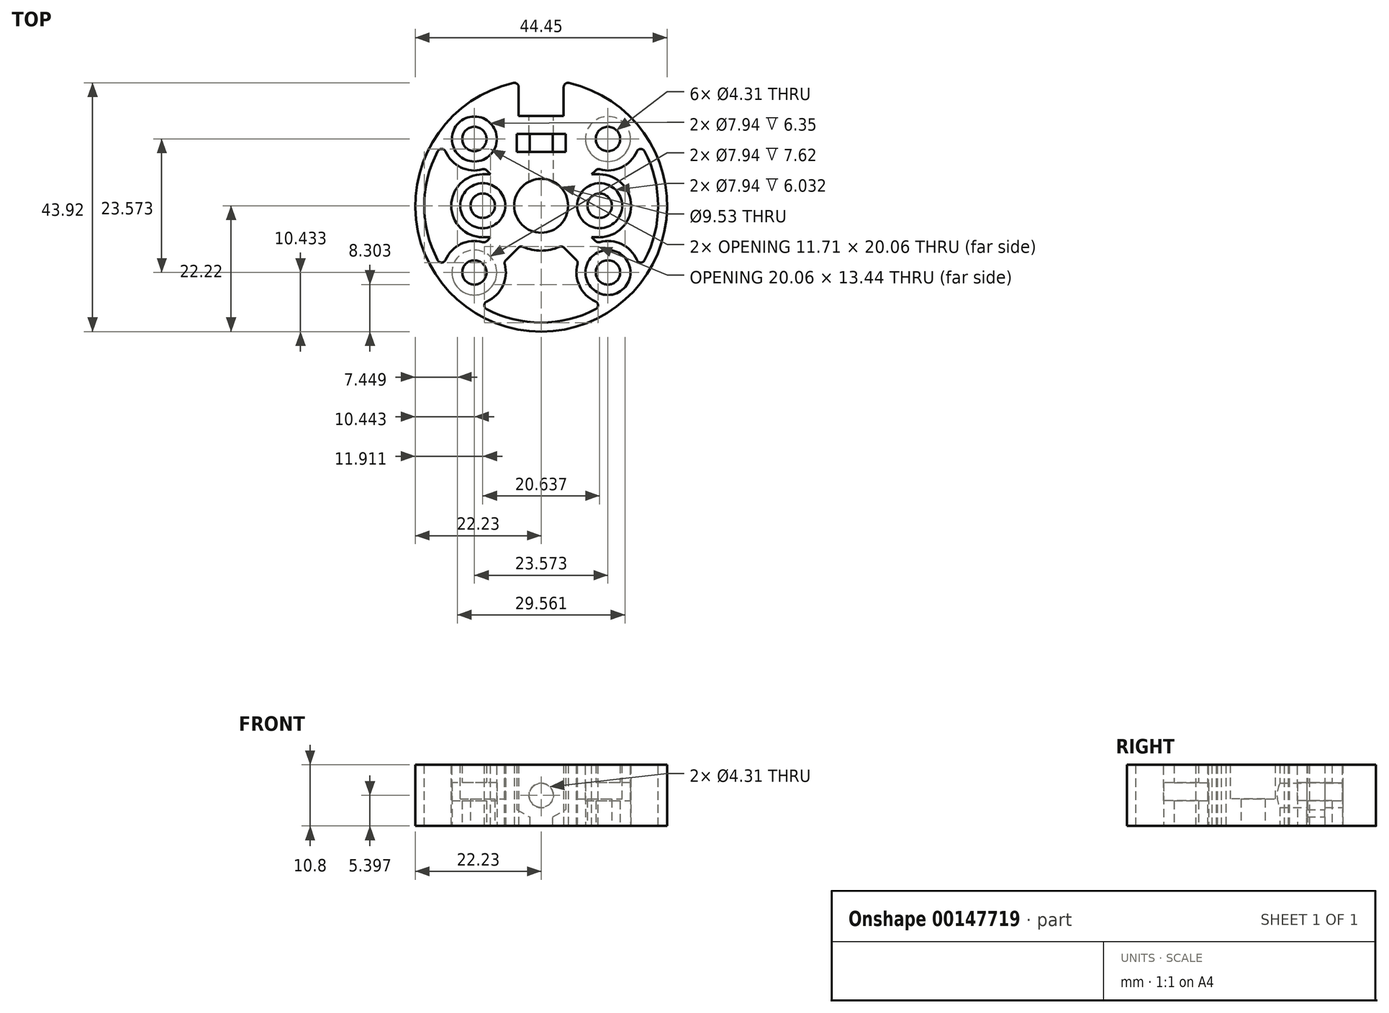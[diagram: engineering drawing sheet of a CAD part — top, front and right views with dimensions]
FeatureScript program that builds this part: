
annotation { "Feature Type Name" : "Feature", "Feature Type Description" : "" }
export const myFeature = defineFeature(function(context is Context, id is Id, definition is map)
    precondition{}
    {
        {
            var Q0;
            Q0=qCreatedBy(makeId("Top.planeOp"),FACE);
            var sketch = newSketch(context, id + "F0", { "sketchPlane" : qUnion([Q0])});
            skLineSegment(sketch, "E0.bottom", {"start": v(11.79, 11.79) * mm, "end": v(-11.79, 11.79) * mm, "construction": true});
            skLineSegment(sketch, "E0.top", {"start": v(11.79, -11.79) * mm, "end": v(-11.79, -11.79) * mm, "construction": true});
            skLineSegment(sketch, "E0.left", {"start": v(11.79, 11.79) * mm, "end": v(11.79, -11.79) * mm, "construction": true});
            skLineSegment(sketch, "E0.right", {"start": v(-11.79, 11.79) * mm, "end": v(-11.79, -11.79) * mm, "construction": true});
            skPoint(sketch, "E0.middle", {"position": v(0, 0) * mm});
            skCircle(sketch, "E1", {"center": v(-11.79, 11.79) * mm, "radius": 5.56 * mm, "construction": true});
            skLineSegment(sketch, "E2", {"start": v(0, 4.76) * mm, "end": v(0, 15.88) * mm});
            skLineSegment(sketch, "E3.bottom", {"start": v(-3.97, 21.87) * mm, "end": v(3.97, 21.87) * mm, "construction": true});
            skLineSegment(sketch, "E3.top", {"start": v(-3.97, 15.88) * mm, "end": v(3.97, 15.88) * mm});
            skLineSegment(sketch, "E3.left", {"start": v(-3.97, 21.87) * mm, "end": v(-3.97, 15.88) * mm});
            skLineSegment(sketch, "E3.right", {"start": v(3.97, 21.87) * mm, "end": v(3.97, 15.88) * mm});
            skArc(sketch, "E4", {"start": v(-3.97, 21.87) * mm, "mid": v(0, -22.22) * mm, "end": v(3.97, 21.87) * mm});
            skCircle(sketch, "E5", {"center": v(-11.79, 11.79) * mm, "radius": 2.15 * mm});
            skCircle(sketch, "E6", {"center": v(-11.79, -11.79) * mm, "radius": 2.15 * mm});
            skCircle(sketch, "E7", {"center": v(11.79, -11.79) * mm, "radius": 2.15 * mm});
            skCircle(sketch, "E8", {"center": v(11.79, 11.79) * mm, "radius": 2.15 * mm});
            skCircle(sketch, "E9", {"center": v(0, 0) * mm, "radius": 4.76 * mm});
            skLineSegment(sketch, "E10", {"start": v(0, 0) * mm, "end": v(0, 3.17) * mm, "construction": true});
            skLineSegment(sketch, "E11", {"start": v(0, 3.17) * mm, "end": v(0, 4.76) * mm, "construction": true});
            skLineSegment(sketch, "E12", {"start": v(-10.32, 0) * mm, "end": v(10.32, 0) * mm, "construction": true});
            skCircle(sketch, "E13", {"center": v(-10.32, 0) * mm, "radius": 2.15 * mm});
            skCircle(sketch, "E14", {"center": v(10.32, 0) * mm, "radius": 2.15 * mm});
            skSolve(sketch);
        }
        {
            var Q0;
            Q0=qSketchRegion(id+"F0",true);
            extrude(context, id + "F1", {"entities" : qUnion([Q0]), "depth" : 10.8 * mm});
        }
        {
            var Q0;
            Q0=makeQuery(id+"F1.opExtrude","SWEPT_FACE",FACE,{"disambiguationData":[OSD([sQuery(id+"F0.wireOp",EDGE,"E3.top")])]});
            var sketch = newSketch(context, id + "F2", { "sketchPlane" : qUnion([Q0])});
            skLineSegment(sketch, "E15", {"start": v(0, 10.8) * mm, "end": v(0, 0) * mm, "construction": true});
            skCircle(sketch, "E16", {"center": v(0, 5.4) * mm, "radius": 2.15 * mm});
            skSolve(sketch);
        }
        {
            var Q0;
            Q0=qSketchRegion(id+"F2",true);
            var Q1;
            Q1=makeQuery(id+"F1.opExtrude","SWEPT_FACE",FACE,{"disambiguationData":[OSD([sQuery(id+"F0.wireOp",EDGE,"E9")])]});
            extrude(context, id + "F3", {"entities" : qUnion([Q0]), "operationType" : NewBodyOperationType.REMOVE, "endBound" : BoundingType.UP_TO_SURFACE, "oppositeDirection" : true, "endBoundEntityFace" : qUnion([Q1]), "depth" : 25.4 * mm});
        }
        {
            var Q0;
            Q0=makeQuery(id+"F1.opExtrude","CAP_FACE",FACE,{"disambiguationData":[OSD([sQuery(id+"F0.wireOp",EDGE,"zcYoioO2-fyPR-UuhC-Hgss-rbXFzuCLLck7"),sQuery(id+"F0.wireOp",EDGE,"E3.top"),sQuery(id+"F0.wireOp",EDGE,"E3.left"),sQuery(id+"F0.wireOp",EDGE,"E3.right"),sQuery(id+"F0.wireOp",EDGE,"E4"),sQuery(id+"F0.wireOp",EDGE,"E5"),sQuery(id+"F0.wireOp",EDGE,"E6"),sQuery(id+"F0.wireOp",EDGE,"E7"),sQuery(id+"F0.wireOp",EDGE,"E8")])],"isStart":true});
            cPlane(context, id + "F4", {"entities" : qUnion([Q0]), "cplaneType" : CPlaneType.OFFSET, "offset" : 4.44 * mm, "oppositeDirection" : true, "width" : 152.4 * mm, "height" : 152.4 * mm});
        }
        {
            var Q0;
            Q0=makeQuery(id+"F1.opExtrude","CAP_FACE",FACE,{"disambiguationData":[OSD([sQuery(id+"F0.wireOp",EDGE,"zcYoioO2-fyPR-UuhC-Hgss-rbXFzuCLLck7"),sQuery(id+"F0.wireOp",EDGE,"E3.top"),sQuery(id+"F0.wireOp",EDGE,"E3.left"),sQuery(id+"F0.wireOp",EDGE,"E3.right"),sQuery(id+"F0.wireOp",EDGE,"E4"),sQuery(id+"F0.wireOp",EDGE,"E5"),sQuery(id+"F0.wireOp",EDGE,"E6"),sQuery(id+"F0.wireOp",EDGE,"E7"),sQuery(id+"F0.wireOp",EDGE,"E8")])],"isStart":false});
            cPlane(context, id + "F5", {"entities" : qUnion([Q0]), "cplaneType" : CPlaneType.OFFSET, "offset" : 3.17 * mm, "oppositeDirection" : true, "width" : 152.4 * mm, "height" : 152.4 * mm});
        }
        {
            var Q0;
            Q0=makeQuery(id+"F1.opExtrude","CAP_FACE",FACE,{"disambiguationData":[OSD([sQuery(id+"F0.wireOp",EDGE,"zcYoioO2-fyPR-UuhC-Hgss-rbXFzuCLLck7"),sQuery(id+"F0.wireOp",EDGE,"E3.top"),sQuery(id+"F0.wireOp",EDGE,"E3.left"),sQuery(id+"F0.wireOp",EDGE,"E3.right"),sQuery(id+"F0.wireOp",EDGE,"E4"),sQuery(id+"F0.wireOp",EDGE,"E5"),sQuery(id+"F0.wireOp",EDGE,"E6"),sQuery(id+"F0.wireOp",EDGE,"E7"),sQuery(id+"F0.wireOp",EDGE,"E8")])],"isStart":false});
            var sketch = newSketch(context, id + "F6", { "sketchPlane" : qUnion([Q0])});
            skCircle(sketch, "E17", {"center": v(-11.79, 11.79) * mm, "radius": 3.97 * mm});
            skCircle(sketch, "E18", {"center": v(11.79, -11.79) * mm, "radius": 3.97 * mm});
            skSolve(sketch);
        }
        {
            var Q0;
            Q0=qSketchRegion(id+"F6",true);
            var Q1;
            Q1=qCreatedBy(id+"F4.planeOp",FACE);
            extrude(context, id + "F7", {"entities" : qUnion([Q0]), "operationType" : NewBodyOperationType.REMOVE, "endBound" : BoundingType.UP_TO_SURFACE, "oppositeDirection" : true, "endBoundEntityFace" : qUnion([Q1]), "depth" : 25.4 * mm});
        }
        {
            var Q0;
            Q0=makeQuery(id+"F1.opExtrude","CAP_FACE",FACE,{"disambiguationData":[OSD([sQuery(id+"F0.wireOp",EDGE,"zcYoioO2-fyPR-UuhC-Hgss-rbXFzuCLLck7"),sQuery(id+"F0.wireOp",EDGE,"E3.top"),sQuery(id+"F0.wireOp",EDGE,"E3.left"),sQuery(id+"F0.wireOp",EDGE,"E3.right"),sQuery(id+"F0.wireOp",EDGE,"E4"),sQuery(id+"F0.wireOp",EDGE,"E5"),sQuery(id+"F0.wireOp",EDGE,"E6"),sQuery(id+"F0.wireOp",EDGE,"E7"),sQuery(id+"F0.wireOp",EDGE,"E8")])],"isStart":true});
            var sketch = newSketch(context, id + "F8", { "sketchPlane" : qUnion([Q0])});
            skCircle(sketch, "E19", {"center": v(11.79, -11.79) * mm, "radius": 3.97 * mm});
            skCircle(sketch, "E20", {"center": v(-11.79, 11.79) * mm, "radius": 3.97 * mm});
            skSolve(sketch);
        }
        {
            var Q0;
            Q0=qSketchRegion(id+"F8",true);
            var Q1;
            Q1=qCreatedBy(id+"F5.planeOp",FACE);
            extrude(context, id + "F9", {"entities" : qUnion([Q0]), "operationType" : NewBodyOperationType.REMOVE, "endBound" : BoundingType.UP_TO_SURFACE, "oppositeDirection" : true, "endBoundEntityFace" : qUnion([Q1]), "depth" : 25.4 * mm});
        }
        {
            var Q0;
            Q0=makeQuery(id+"F1.opExtrude","CAP_FACE",FACE,{"disambiguationData":[OSD([sQuery(id+"F0.wireOp",EDGE,"zcYoioO2-fyPR-UuhC-Hgss-rbXFzuCLLck7"),sQuery(id+"F0.wireOp",EDGE,"E3.top"),sQuery(id+"F0.wireOp",EDGE,"E3.left"),sQuery(id+"F0.wireOp",EDGE,"E3.right"),sQuery(id+"F0.wireOp",EDGE,"E4"),sQuery(id+"F0.wireOp",EDGE,"E5"),sQuery(id+"F0.wireOp",EDGE,"E6"),sQuery(id+"F0.wireOp",EDGE,"E7"),sQuery(id+"F0.wireOp",EDGE,"E8")])],"isStart":false});
            var sketch = newSketch(context, id + "F10", { "sketchPlane" : qUnion([Q0])});
            skArc(sketch, "E21", {"start": v(-17.31, 11.23) * mm, "mid": v(-14.76, 7.1) * mm, "end": v(-9.92, 6.55) * mm});
            skArc(sketch, "E22", {"start": v(-17.31, 11.23) * mm, "mid": v(-20.64, 0) * mm, "end": v(-17.31, -11.23) * mm});
            skArc(sketch, "E23", {"start": v(-9.92, -6.55) * mm, "mid": v(-14.76, -7.1) * mm, "end": v(-17.31, -11.23) * mm});
            skLineSegment(sketch, "E24", {"start": v(-11.79, 11.79) * mm, "end": v(-8.24, 8.24) * mm, "construction": true});
            skLineSegment(sketch, "E25.bottom", {"start": v(-9.92, 6.55) * mm, "end": v(-8.92, 5.56) * mm});
            skLineSegment(sketch, "E25.top", {"start": v(-6.55, 9.92) * mm, "end": v(-5.56, 8.92) * mm, "construction": true});
            skLineSegment(sketch, "E25.left", {"start": v(-9.92, 6.55) * mm, "end": v(-6.55, 9.92) * mm, "construction": true});
            skLineSegment(sketch, "E25.right", {"start": v(-8.92, 5.56) * mm, "end": v(-5.56, 8.92) * mm, "construction": true});
            skLineSegment(sketch, "E26", {"start": v(0, 0) * mm, "end": v(-7.24, 7.24) * mm, "construction": true});
            skLineSegment(sketch, "E27.bottom", {"start": v(-9.92, -6.55) * mm, "end": v(-8.92, -5.56) * mm});
            skLineSegment(sketch, "E27.top", {"start": v(-6.55, -9.92) * mm, "end": v(-5.56, -8.92) * mm, "construction": true});
            skLineSegment(sketch, "E27.left", {"start": v(-9.92, -6.55) * mm, "end": v(-6.55, -9.92) * mm, "construction": true});
            skLineSegment(sketch, "E27.right", {"start": v(-8.92, -5.56) * mm, "end": v(-5.56, -8.92) * mm, "construction": true});
            skLineSegment(sketch, "E28", {"start": v(-11.79, -11.79) * mm, "end": v(-8.24, -8.24) * mm, "construction": true});
            skLineSegment(sketch, "E29", {"start": v(-7.24, -7.24) * mm, "end": v(0, 0) * mm, "construction": true});
            skLineSegment(sketch, "E30.bottom", {"start": v(-8.92, -5.56) * mm, "end": v(-10.32, -5.56) * mm});
            skLineSegment(sketch, "E30.top", {"start": v(-8.92, 5.56) * mm, "end": v(-10.32, 5.56) * mm});
            skLineSegment(sketch, "E30.left", {"start": v(-8.92, -5.56) * mm, "end": v(-8.92, 5.56) * mm, "construction": true});
            skLineSegment(sketch, "E30.right", {"start": v(-10.32, -5.56) * mm, "end": v(-10.32, 5.56) * mm, "construction": true});
            skArc(sketch, "E31", {"start": v(-10.32, 5.56) * mm, "mid": v(-15.88, 0) * mm, "end": v(-10.32, -5.56) * mm});
            skSolve(sketch);
        }
        {
            var Q0;
            Q0=qSketchRegion(id+"F10",true);
            var Q1;
            Q1=makeQuery(id+"F1.opExtrude","CAP_FACE",FACE,{"disambiguationData":[OSD([sQuery(id+"F0.wireOp",EDGE,"zcYoioO2-fyPR-UuhC-Hgss-rbXFzuCLLck7"),sQuery(id+"F0.wireOp",EDGE,"E3.top"),sQuery(id+"F0.wireOp",EDGE,"E3.left"),sQuery(id+"F0.wireOp",EDGE,"E3.right"),sQuery(id+"F0.wireOp",EDGE,"E4"),sQuery(id+"F0.wireOp",EDGE,"E5"),sQuery(id+"F0.wireOp",EDGE,"E6"),sQuery(id+"F0.wireOp",EDGE,"E7"),sQuery(id+"F0.wireOp",EDGE,"E8")])],"isStart":true});
            extrude(context, id + "F11", {"entities" : qUnion([Q0]), "operationType" : NewBodyOperationType.REMOVE, "endBound" : BoundingType.UP_TO_SURFACE, "oppositeDirection" : true, "endBoundEntityFace" : qUnion([Q1]), "depth" : 25.4 * mm});
        }
        {
            var Q0;
            Q0=makeQuery(id+"F1.opExtrude","SWEPT_FACE",FACE,{"disambiguationData":[OSD([sQuery(id+"F0.wireOp",EDGE,"E3.top")])]});
            var sketch = newSketch(context, id + "F12", { "sketchPlane" : qUnion([Q0])});
            skLineSegment(sketch, "E32", {"start": v(0, 0) * mm, "end": v(0, 10.8) * mm, "construction": true});
            skCircle(sketch, "E33", {"center": v(0, 5.4) * mm, "radius": 2.15 * mm});
            skSolve(sketch);
        }
        {
            var Q0;
            Q0=qSketchRegion(id+"F12",true);
            var Q1;
            Q1=makeQuery(id+"F1.opExtrude","SWEPT_FACE",FACE,{"disambiguationData":[OSD([sQuery(id+"F0.wireOp",EDGE,"E9")])]});
            extrude(context, id + "F13", {"entities" : qUnion([Q0]), "operationType" : NewBodyOperationType.REMOVE, "endBound" : BoundingType.UP_TO_SURFACE, "oppositeDirection" : true, "endBoundEntityFace" : qUnion([Q1]), "depth" : 25.4 * mm});
        }
        {
            var Q0;
            Q0=makeQuery(id+"F11.boolean.opBoolean","COPY",EDGE,{"derivedFrom":makeQuery(id+"F11.opExtrude","SWEPT_EDGE",EDGE,{"disambiguationData":[OSD([sQuery(id+"F10.wireOp",EDGE,"E22"),sQuery(id+"F10.wireOp",EDGE,"E23")])]})});
            var Q1;
            Q1=makeQuery(id+"FlX28BifZiOdl7F_1.1.F11.boolean.opBoolean","COPY",EDGE,{"derivedFrom":makeQuery(id+"FlX28BifZiOdl7F_1.1.F11.opExtrude","SWEPT_EDGE",EDGE,{"disambiguationData":[OSD([sQuery(id+"F10.wireOp",EDGE,"E21"),sQuery(id+"F10.wireOp",EDGE,"E22")])]})});
            var Q2;
            Q2=makeQuery(id+"F11.boolean.opBoolean","COPY",EDGE,{"derivedFrom":makeQuery(id+"F11.opExtrude","SWEPT_EDGE",EDGE,{"disambiguationData":[OSD([sQuery(id+"F10.wireOp",EDGE,"E21"),sQuery(id+"F10.wireOp",EDGE,"E22")])]})});
            var Q3;
            Q3=makeQuery(id+"FlX28BifZiOdl7F_1.1.F11.boolean.opBoolean","COPY",EDGE,{"derivedFrom":makeQuery(id+"FlX28BifZiOdl7F_1.1.F11.opExtrude","SWEPT_EDGE",EDGE,{"disambiguationData":[OSD([sQuery(id+"F10.wireOp",EDGE,"E22"),sQuery(id+"F10.wireOp",EDGE,"E23")])]})});
            var Q4;
            Q4=makeQuery(id+"FlX28BifZiOdl7F_1.2.F11.boolean.opBoolean","COPY",EDGE,{"derivedFrom":makeQuery(id+"FlX28BifZiOdl7F_1.2.F11.opExtrude","SWEPT_EDGE",EDGE,{"disambiguationData":[OSD([sQuery(id+"F10.wireOp",EDGE,"E21"),sQuery(id+"F10.wireOp",EDGE,"E22")])]})});
            var Q5;
            Q5=makeQuery(id+"FlX28BifZiOdl7F_1.2.F11.boolean.opBoolean","COPY",EDGE,{"derivedFrom":makeQuery(id+"FlX28BifZiOdl7F_1.2.F11.opExtrude","SWEPT_EDGE",EDGE,{"disambiguationData":[OSD([sQuery(id+"F10.wireOp",EDGE,"E22"),sQuery(id+"F10.wireOp",EDGE,"E23")])]})});
            var Q6;
            Q6=makeQuery(id+"FWKm7hUAplBFvIC_1.boolean.opBoolean","COPY",EDGE,{"derivedFrom":makeQuery(id+"FWKm7hUAplBFvIC_1.opExtrude","SWEPT_EDGE",EDGE,{"disambiguationData":[OSD([sQuery(id+"FmsORHBhZr1tewJ_1.wireOp",EDGE,"mSwwP5tA-oHFi-Nunc-EFce-jrX3o5ssh5km"),sQuery(id+"FmsORHBhZr1tewJ_1.wireOp",EDGE,"tS8HIu0J-R6c9-g4Ys-TcZS-SzFWZ2vIbcui")])]})});
            var Q7;
            Q7=makeQuery(id+"F1.opExtrude","SWEPT_EDGE",EDGE,{"disambiguationData":[OSD([sQuery(id+"F0.wireOp",EDGE,"E3.right"),sQuery(id+"F0.wireOp",EDGE,"E4")])]});
            var Q8;
            Q8=makeQuery(id+"F1.opExtrude","SWEPT_EDGE",EDGE,{"disambiguationData":[OSD([sQuery(id+"F0.wireOp",EDGE,"E3.left"),sQuery(id+"F0.wireOp",EDGE,"E4")])]});
            var Q9;
            Q9=makeQuery(id+"FWKm7hUAplBFvIC_1.boolean.opBoolean","COPY",EDGE,{"derivedFrom":makeQuery(id+"FWKm7hUAplBFvIC_1.opExtrude","SWEPT_EDGE",EDGE,{"disambiguationData":[OSD([sQuery(id+"FmsORHBhZr1tewJ_1.wireOp",EDGE,"cfy8YxAp-tAZO-ZDde-LiWi-n8fxJ0o6mKEZ"),sQuery(id+"FmsORHBhZr1tewJ_1.wireOp",EDGE,"LdsrjSXB-VNQW-crlt-P9au-F7ZgSEs9XLl7")])]})});
            var Q10;
            Q10=makeQuery(id+"F11.boolean.opBoolean","COPY",EDGE,{"derivedFrom":makeQuery(id+"F11.opExtrude","SWEPT_EDGE",EDGE,{"disambiguationData":[OSD([sQuery(id+"F10.wireOp",EDGE,"E21"),sQuery(id+"F10.wireOp",EDGE,"XyXLIx7K-ZfDS-UaZi-ZrPZ-9wLtyjpZrvfo")])]})});
            var Q11;
            Q11=makeQuery(id+"F11.boolean.opBoolean","COPY",EDGE,{"derivedFrom":makeQuery(id+"F11.opExtrude","SWEPT_EDGE",EDGE,{"disambiguationData":[OSD([sQuery(id+"F10.wireOp",EDGE,"E23"),sQuery(id+"F10.wireOp",EDGE,"XyXLIx7K-ZfDS-UaZi-ZrPZ-9wLtyjpZrvfo")])]})});
            var Q12;
            Q12=makeQuery(id+"FlX28BifZiOdl7F_1.1.F11.boolean.opBoolean","COPY",EDGE,{"derivedFrom":makeQuery(id+"FlX28BifZiOdl7F_1.1.F11.opExtrude","SWEPT_EDGE",EDGE,{"disambiguationData":[OSD([sQuery(id+"F10.wireOp",EDGE,"E21"),sQuery(id+"F10.wireOp",EDGE,"XyXLIx7K-ZfDS-UaZi-ZrPZ-9wLtyjpZrvfo")])]})});
            var Q13;
            Q13=makeQuery(id+"FlX28BifZiOdl7F_1.1.F11.boolean.opBoolean","COPY",EDGE,{"derivedFrom":makeQuery(id+"FlX28BifZiOdl7F_1.1.F11.opExtrude","SWEPT_EDGE",EDGE,{"disambiguationData":[OSD([sQuery(id+"F10.wireOp",EDGE,"E23"),sQuery(id+"F10.wireOp",EDGE,"XyXLIx7K-ZfDS-UaZi-ZrPZ-9wLtyjpZrvfo")])]})});
            var Q14;
            Q14=makeQuery(id+"FlX28BifZiOdl7F_1.2.F11.boolean.opBoolean","COPY",EDGE,{"derivedFrom":makeQuery(id+"FlX28BifZiOdl7F_1.2.F11.opExtrude","SWEPT_EDGE",EDGE,{"disambiguationData":[OSD([sQuery(id+"F10.wireOp",EDGE,"E21"),sQuery(id+"F10.wireOp",EDGE,"XyXLIx7K-ZfDS-UaZi-ZrPZ-9wLtyjpZrvfo")])]})});
            var Q15;
            Q15=makeQuery(id+"FlX28BifZiOdl7F_1.2.F11.boolean.opBoolean","COPY",EDGE,{"derivedFrom":makeQuery(id+"FlX28BifZiOdl7F_1.2.F11.opExtrude","SWEPT_EDGE",EDGE,{"disambiguationData":[OSD([sQuery(id+"F10.wireOp",EDGE,"E23"),sQuery(id+"F10.wireOp",EDGE,"XyXLIx7K-ZfDS-UaZi-ZrPZ-9wLtyjpZrvfo")])]})});
            fillet(context, id + "F14", {"entities" : qUnion([Q0, Q1, Q2, Q3, Q4, Q5, Q6, Q7, Q8, Q9, Q10, Q11, Q12, Q13, Q14, Q15]), "radius" : 0.76 * mm, "tangentPropagation" : true, "allowEdgeOverflow" : false});
        }
        {
            var Q0;
            Q0=makeQuery(id+"F14.opFillet","BLEND_FACE",FACE,{"disambiguationData":[OSD([sQuery(id+"F10.wireOp",EDGE,"E21"),sQuery(id+"F10.wireOp",EDGE,"E22")])]});
            var Q1;
            Q1=makeQuery(id+"F11.boolean.opBoolean","COPY",FACE,{"derivedFrom":makeQuery(id+"F11.opExtrude","SWEPT_FACE",FACE,{"disambiguationData":[OSD([sQuery(id+"F10.wireOp",EDGE,"E21")])]})});
            var Q2;
            Q2=makeQuery(id+"F14.opFillet","BLEND_FACE",FACE,{"disambiguationData":[OSD([sQuery(id+"F10.wireOp",EDGE,"E21"),sQuery(id+"F10.wireOp",EDGE,"E25.bottom")])]});
            var Q3;
            Q3=makeQuery(id+"F11.boolean.opBoolean","COPY",FACE,{"derivedFrom":makeQuery(id+"F11.opExtrude","SWEPT_FACE",FACE,{"disambiguationData":[OSD([sQuery(id+"F10.wireOp",EDGE,"E25.bottom")])]})});
            var Q4;
            Q4=makeQuery(id+"F11.boolean.opBoolean","COPY",FACE,{"derivedFrom":makeQuery(id+"F11.opExtrude","SWEPT_FACE",FACE,{"disambiguationData":[OSD([sQuery(id+"F10.wireOp",EDGE,"D47F1shm-cYHo-DtrT-ayz3-ePBbmINjOO7p")])]})});
            var Q5;
            Q5=makeQuery(id+"F11.boolean.opBoolean","COPY",FACE,{"derivedFrom":makeQuery(id+"F11.opExtrude","SWEPT_FACE",FACE,{"disambiguationData":[OSD([sQuery(id+"F10.wireOp",EDGE,"E30.top")])]})});
            var Q6;
            Q6=makeQuery(id+"F11.boolean.opBoolean","COPY",FACE,{"derivedFrom":makeQuery(id+"F11.opExtrude","SWEPT_FACE",FACE,{"disambiguationData":[OSD([sQuery(id+"F10.wireOp",EDGE,"E31")])]})});
            var Q7;
            Q7=makeQuery(id+"F11.boolean.opBoolean","COPY",FACE,{"derivedFrom":makeQuery(id+"F11.opExtrude","SWEPT_FACE",FACE,{"disambiguationData":[OSD([sQuery(id+"F10.wireOp",EDGE,"E30.bottom")])]})});
            var Q8;
            Q8=makeQuery(id+"F11.boolean.opBoolean","COPY",FACE,{"derivedFrom":makeQuery(id+"F11.opExtrude","SWEPT_FACE",FACE,{"disambiguationData":[OSD([sQuery(id+"F10.wireOp",EDGE,"sPoPCCh0-1323-NAZL-0xvt-ILVy8YAv08VG")])]})});
            var Q9;
            Q9=makeQuery(id+"F11.boolean.opBoolean","COPY",FACE,{"derivedFrom":makeQuery(id+"F11.opExtrude","SWEPT_FACE",FACE,{"disambiguationData":[OSD([sQuery(id+"F10.wireOp",EDGE,"E27.bottom")])]})});
            var Q10;
            Q10=makeQuery(id+"F14.opFillet","BLEND_FACE",FACE,{"disambiguationData":[OSD([sQuery(id+"F10.wireOp",EDGE,"E23"),sQuery(id+"F10.wireOp",EDGE,"E27.bottom")])]});
            var Q11;
            Q11=makeQuery(id+"F11.boolean.opBoolean","COPY",FACE,{"derivedFrom":makeQuery(id+"F11.opExtrude","SWEPT_FACE",FACE,{"disambiguationData":[OSD([sQuery(id+"F10.wireOp",EDGE,"E23")])]})});
            var Q12;
            Q12=makeQuery(id+"F14.opFillet","BLEND_FACE",FACE,{"disambiguationData":[OSD([sQuery(id+"F10.wireOp",EDGE,"E22"),sQuery(id+"F10.wireOp",EDGE,"E23")])]});
            var Q13;
            Q13=makeQuery(id+"F11.boolean.opBoolean","COPY",FACE,{"derivedFrom":makeQuery(id+"F11.opExtrude","SWEPT_FACE",FACE,{"disambiguationData":[OSD([sQuery(id+"F10.wireOp",EDGE,"E22")])]})});
            var Q14;
            Q14=makeQuery(id+"F1.opExtrude","SWEPT_FACE",FACE,{"disambiguationData":[OSD([sQuery(id+"F0.wireOp",EDGE,"E9")])]});
            circularPattern(context, id + "F15", {"patternType" : PatternType.FACE, "faces" : qUnion([Q0, Q1, Q2, Q3, Q4, Q5, Q6, Q7, Q8, Q9, Q10, Q11, Q12, Q13]), "axis" : qUnion([Q14]), "angle" : 180 * degree, "instanceCount" : 2});
        }
        {
            var Q0;
            Q0=makeQuery(id+"F1.opExtrude","SWEPT_FACE",FACE,{"disambiguationData":[OSD([sQuery(id+"F0.wireOp",EDGE,"E3.top")])]});
            cPlane(context, id + "F16", {"entities" : qUnion([Q0]), "cplaneType" : CPlaneType.OFFSET, "offset" : 3.17 * mm, "oppositeDirection" : true, "width" : 152.4 * mm, "height" : 152.4 * mm});
        }
        {
            var Q0;
            Q0=qCreatedBy(id+"F16.planeOp",FACE);
            var sketch = newSketch(context, id + "F17", { "sketchPlane" : qUnion([Q0])});
            skCircle(sketch, "E34.cCircle", {"center": v(0, 5.4) * mm, "radius": 4.32 * mm, "construction": true});
            skLineSegment(sketch, "E34.0", {"start": v(-4.32, 2.9) * mm, "end": v(-4.32, 7.9) * mm});
            skLineSegment(sketch, "E34.1", {"start": v(-4.32, 7.9) * mm, "end": v(0, 10.38) * mm, "construction": true});
            skLineSegment(sketch, "E34.2", {"start": v(0, 10.38) * mm, "end": v(4.32, 7.9) * mm, "construction": true});
            skLineSegment(sketch, "E34.3", {"start": v(4.32, 7.9) * mm, "end": v(4.32, 2.9) * mm});
            skLineSegment(sketch, "E34.4", {"start": v(4.32, 2.9) * mm, "end": v(0, 0.41) * mm});
            skLineSegment(sketch, "E34.5", {"start": v(0, 0.41) * mm, "end": v(-4.32, 2.9) * mm});
            skPoint(sketch, "E34.0.midPoint", {"position": v(-4.32, 5.4) * mm});
            skLineSegment(sketch, "E35", {"start": v(4.32, 7.9) * mm, "end": v(4.32, 10.8) * mm});
            skLineSegment(sketch, "E36", {"start": v(4.32, 10.8) * mm, "end": v(-4.32, 10.8) * mm});
            skLineSegment(sketch, "E37", {"start": v(-4.32, 10.8) * mm, "end": v(-4.32, 7.9) * mm});
            skLineSegment(sketch, "E38", {"start": v(2.04, 1.59) * mm, "end": v(2.04, 0) * mm});
            skLineSegment(sketch, "E39", {"start": v(2.04, 0) * mm, "end": v(-2.04, 0) * mm});
            skLineSegment(sketch, "E40", {"start": v(-2.04, 0) * mm, "end": v(-2.04, 1.59) * mm});
            skSolve(sketch);
        }
        {
            var Q0;
            Q0=qSketchRegion(id+"F17",true);
            extrude(context, id + "F18", {"entities" : qUnion([Q0]), "operationType" : NewBodyOperationType.REMOVE, "oppositeDirection" : true, "depth" : 3.17 * mm});
        }
        {
            var Q0;
            Q0=makeQuery(id+"F1.opExtrude","CAP_FACE",FACE,{"disambiguationData":[OSD([sQuery(id+"F0.wireOp",EDGE,"E3.top"),sQuery(id+"F0.wireOp",EDGE,"E3.left"),sQuery(id+"F0.wireOp",EDGE,"E3.right"),sQuery(id+"F0.wireOp",EDGE,"E4"),sQuery(id+"F0.wireOp",EDGE,"E5"),sQuery(id+"F0.wireOp",EDGE,"E6"),sQuery(id+"F0.wireOp",EDGE,"E7"),sQuery(id+"F0.wireOp",EDGE,"E8"),sQuery(id+"F0.wireOp",EDGE,"E9"),sQuery(id+"F0.wireOp",EDGE,"E13"),sQuery(id+"F0.wireOp",EDGE,"E14")])],"isStart":false});
            var sketch = newSketch(context, id + "F19", { "sketchPlane" : qUnion([Q0])});
            skCircle(sketch, "E41", {"center": v(-10.32, 0) * mm, "radius": 3.97 * mm});
            skCircle(sketch, "E42", {"center": v(10.32, 0) * mm, "radius": 3.97 * mm});
            skSolve(sketch);
        }
        {
            var Q0;
            Q0=makeQuery(id+"F1.opExtrude","CAP_FACE",FACE,{"disambiguationData":[OSD([sQuery(id+"F0.wireOp",EDGE,"E3.top"),sQuery(id+"F0.wireOp",EDGE,"E3.left"),sQuery(id+"F0.wireOp",EDGE,"E3.right"),sQuery(id+"F0.wireOp",EDGE,"E4"),sQuery(id+"F0.wireOp",EDGE,"E5"),sQuery(id+"F0.wireOp",EDGE,"E6"),sQuery(id+"F0.wireOp",EDGE,"E7"),sQuery(id+"F0.wireOp",EDGE,"E8"),sQuery(id+"F0.wireOp",EDGE,"E9"),sQuery(id+"F0.wireOp",EDGE,"E13"),sQuery(id+"F0.wireOp",EDGE,"E14")])],"isStart":true});
            cPlane(context, id + "F20", {"entities" : qUnion([Q0]), "cplaneType" : CPlaneType.OFFSET, "offset" : 4.76 * mm, "oppositeDirection" : true, "width" : 152.4 * mm, "height" : 152.4 * mm});
        }
        {
            var Q0;
            Q0=makeQuery(id+"F19.imprint","IMPRINT",FACE,{"disambiguationData":[TD([[makeQuery(id+"F19.imprint","IMPRINT",EDGE,{"derivedFrom":sQuery(id+"F19.wireOp",EDGE,"E41")}),1.0]])]});
            var Q1;
            Q1=makeQuery(id+"F19.imprint","IMPRINT",FACE,{"disambiguationData":[TD([[makeQuery(id+"F19.imprint","IMPRINT",EDGE,{"derivedFrom":sQuery(id+"F19.wireOp",EDGE,"E42")}),1.0]])]});
            var Q2;
            Q2=sQuery(id+"F19.wireOp",EDGE,"E41");
            var Q3;
            Q3=sQuery(id+"F19.wireOp",EDGE,"E42");
            var Q4;
            Q4=qCreatedBy(id+"F20.planeOp",FACE);
            extrude(context, id + "F21", {"entities" : qUnion([Q0, Q1]), "operationType" : NewBodyOperationType.REMOVE, "surfaceEntities" : qUnion([Q2, Q3]), "endBound" : BoundingType.UP_TO_SURFACE, "oppositeDirection" : true, "endBoundEntityFace" : qUnion([Q4]), "depth" : 25.4 * mm});
        }
        {
            var Q0;
            Q0=makeQuery(id+"F1.opExtrude","CAP_FACE",FACE,{"disambiguationData":[OSD([sQuery(id+"F0.wireOp",EDGE,"E3.top"),sQuery(id+"F0.wireOp",EDGE,"E3.left"),sQuery(id+"F0.wireOp",EDGE,"E3.right"),sQuery(id+"F0.wireOp",EDGE,"E4"),sQuery(id+"F0.wireOp",EDGE,"E5"),sQuery(id+"F0.wireOp",EDGE,"E6"),sQuery(id+"F0.wireOp",EDGE,"E7"),sQuery(id+"F0.wireOp",EDGE,"E8"),sQuery(id+"F0.wireOp",EDGE,"E9"),sQuery(id+"F0.wireOp",EDGE,"E13"),sQuery(id+"F0.wireOp",EDGE,"E14")])],"isStart":false});
            var sketch = newSketch(context, id + "F22", { "sketchPlane" : qUnion([Q0])});
            skLineSegment(sketch, "E43.bottom", {"start": v(-6.55, -9.92) * mm, "end": v(-3.67, -7.04) * mm});
            skLineSegment(sketch, "E43.top", {"start": v(-9.92, -6.55) * mm, "end": v(-7.04, -3.67) * mm, "construction": true});
            skLineSegment(sketch, "E43.left", {"start": v(-3.67, -7.04) * mm, "end": v(-7.04, -3.67) * mm, "construction": true});
            skLineSegment(sketch, "E43.right", {"start": v(-6.55, -9.92) * mm, "end": v(-9.92, -6.55) * mm, "construction": true});
            skArc(sketch, "E44", {"start": v(-11.23, -17.31) * mm, "mid": v(-7.1, -14.76) * mm, "end": v(-6.55, -9.92) * mm});
            skArc(sketch, "E45", {"start": v(-3.67, -7.04) * mm, "mid": v(0, -7.94) * mm, "end": v(3.67, -7.04) * mm});
            skArc(sketch, "E46", {"start": v(6.55, -9.92) * mm, "mid": v(7.1, -14.76) * mm, "end": v(11.23, -17.31) * mm});
            skArc(sketch, "E47", {"start": v(-11.23, -17.31) * mm, "mid": v(0, -20.64) * mm, "end": v(11.23, -17.31) * mm});
            skLineSegment(sketch, "E48.bottom", {"start": v(6.55, -9.92) * mm, "end": v(3.67, -7.04) * mm});
            skLineSegment(sketch, "E48.top", {"start": v(9.92, -6.55) * mm, "end": v(7.04, -3.67) * mm, "construction": true});
            skLineSegment(sketch, "E48.left", {"start": v(6.55, -9.92) * mm, "end": v(9.92, -6.55) * mm, "construction": true});
            skLineSegment(sketch, "E48.right", {"start": v(3.67, -7.04) * mm, "end": v(7.04, -3.67) * mm, "construction": true});
            skSolve(sketch);
        }
        {
            var Q0;
            Q0=qSketchRegion(id+"F22",true);
            var Q1;
            Q1=makeQuery(id+"F1.opExtrude","CAP_FACE",FACE,{"disambiguationData":[OSD([sQuery(id+"F0.wireOp",EDGE,"E3.top"),sQuery(id+"F0.wireOp",EDGE,"E3.left"),sQuery(id+"F0.wireOp",EDGE,"E3.right"),sQuery(id+"F0.wireOp",EDGE,"E4"),sQuery(id+"F0.wireOp",EDGE,"E5"),sQuery(id+"F0.wireOp",EDGE,"E6"),sQuery(id+"F0.wireOp",EDGE,"E7"),sQuery(id+"F0.wireOp",EDGE,"E8"),sQuery(id+"F0.wireOp",EDGE,"E9"),sQuery(id+"F0.wireOp",EDGE,"E13"),sQuery(id+"F0.wireOp",EDGE,"E14")])],"isStart":true});
            extrude(context, id + "F23", {"entities" : qUnion([Q0]), "operationType" : NewBodyOperationType.REMOVE, "endBound" : BoundingType.UP_TO_SURFACE, "oppositeDirection" : true, "endBoundEntityFace" : qUnion([Q1]), "depth" : 25.4 * mm});
        }
        {
            var Q0;
            Q0=makeQuery(id+"F23.boolean.opBoolean","COPY",EDGE,{"derivedFrom":makeQuery(id+"F23.opExtrude","SWEPT_EDGE",EDGE,{"disambiguationData":[OSD([sQuery(id+"F22.wireOp",EDGE,"E45"),sQuery(id+"F22.wireOp",EDGE,"E48.bottom")])]})});
            var Q1;
            Q1=makeQuery(id+"F23.boolean.opBoolean","COPY",EDGE,{"derivedFrom":makeQuery(id+"F23.opExtrude","SWEPT_EDGE",EDGE,{"disambiguationData":[OSD([sQuery(id+"F22.wireOp",EDGE,"E46"),sQuery(id+"F22.wireOp",EDGE,"E48.bottom")])]})});
            var Q2;
            Q2=makeQuery(id+"F23.boolean.opBoolean","COPY",EDGE,{"derivedFrom":makeQuery(id+"F23.opExtrude","SWEPT_EDGE",EDGE,{"disambiguationData":[OSD([sQuery(id+"F22.wireOp",EDGE,"E46"),sQuery(id+"F22.wireOp",EDGE,"E47")])]})});
            var Q3;
            Q3=makeQuery(id+"F23.boolean.opBoolean","COPY",EDGE,{"derivedFrom":makeQuery(id+"F23.opExtrude","SWEPT_EDGE",EDGE,{"disambiguationData":[OSD([sQuery(id+"F22.wireOp",EDGE,"E44"),sQuery(id+"F22.wireOp",EDGE,"E47")])]})});
            var Q4;
            Q4=makeQuery(id+"F23.boolean.opBoolean","COPY",EDGE,{"derivedFrom":makeQuery(id+"F23.opExtrude","SWEPT_EDGE",EDGE,{"disambiguationData":[OSD([sQuery(id+"F22.wireOp",EDGE,"E43.bottom"),sQuery(id+"F22.wireOp",EDGE,"E44")])]})});
            var Q5;
            Q5=makeQuery(id+"F23.boolean.opBoolean","COPY",EDGE,{"derivedFrom":makeQuery(id+"F23.opExtrude","SWEPT_EDGE",EDGE,{"disambiguationData":[OSD([sQuery(id+"F22.wireOp",EDGE,"E43.bottom"),sQuery(id+"F22.wireOp",EDGE,"E45")])]})});
            fillet(context, id + "F24", {"entities" : qUnion([Q0, Q1, Q2, Q3, Q4, Q5]), "radius" : 0.76 * mm, "tangentPropagation" : true, "allowEdgeOverflow" : false});
        }
    });
